# Revit family: NAU_Naughtone_Stng_Hush_LowChair
name_source: partatom
category: Furniture
revit_build: Autodesk Revit 2015 (Build: 20140903_1530(x64)
units: mm (PartAtom-declared; Revit-internal decimal feet)

## types (3) — shared parameters
Additional Materials = Additional material and finish options available. Please contact Naughtone direct for further information.
Assembly Code = E2020200
AssetType = Movable
BIMObjectName = NAU_Naughtone_Seating_Hush_LowChair
BaseMaterial = Aluminum - Gen - Satin
Category = Pr_40_50_12 : Chairs, seats and benches
Color = Various
DurationUnit = year
Finish = Upholstered
IfcExportAs = IfcFurnishingElementType
IfcExportType = CHAIR
Keynote = Pr_40_50_12
MainColor = Various
ManufacturerAddress = Knaresborough Tech Park, Manse Lane, Knaresborough, HG5 8LF
ManufacturerName = Naughtone
ManufacturerURL = www.naughtone.com
NBSDescription = Seating
NBSReference = 45-35-72/352
Name = Seating_Hush_LowChair_Naughtone
NominalHeight = 880 mm  [stored 2.88714 ft]
NominalLength = 760 mm
NominalWidth = 720 mm  [stored 2.3622 ft]
ProductInformation = www.naughtone.com/products/hush-low/
Revision = 1
Shape = Rectangular
Size = 760 x 720 x 880mm
SustainabilityPerformance = FSC certified. FISP certified. ISO 14001
URL = www.naughtone.com
Uniclass2015Code = Pr_40_50_12
Uniclass2015Title = Chairs, seats and benches
Uniclass2015Version = Products v1.10
Version = 1
WarrantyDescription = Request warranty information from naughtone
WarrantyDurationLabor = 5
WarrantyDurationParts = 5
WarrantyDurationUnit = year
zero-valued in all types: Cost

## per-type parameters (varying)
| type | Description | HasSledBase | HasSwivelBase | HasWoodenLegs | ModelReference |
| HULOB4S | Hush Low Chair on 4 Star Base | No | Yes | No | Hush Low Chair on 4 Star Base |
| HULOBWD | Hush Low on Wooden Base | No | No | Yes | Hush Low on Wooden Base |
| HULOBSL | Hush Low Chair with Sled Base | Yes | No | No | Hush Low Chair with Sled Base |

note: column(s) folded — value = type name in every type: Model, ModelNumber

note: [stored X ft] marks values corroborated as IEEE doubles in the binary element streams (Revit-internal decimal feet)

## geometry (parser evidence)
native form markers: Blend x4, Sweep x8
no freeform markers — native parametric forms only
